# Revit family: KingswayGroup_Shlvs_Anti-LigatureWashroomShelfRecessed
name_source: partatom
category: Specialty Equipment
units: mm (PartAtom-declared; Revit-internal decimal feet)

## family parameters
Always vertical = Yes
Cut with Voids When Loaded = No
Part Type = Normal
Room Calculation Point = No
Round Connector Dimension = Use Diameter
Shared = No
Work Plane-Based = No

## types (1)
- KingswayGroup_Shlvs_Anti-LigatureWashroomShelfRecessed
    AssetType = Fixed
    BIMObjectName = KingswayGroup_Shelves_Anti-LigatureWashroomShelfRecessed
    Category = Pr_40_30_78_78:Shelves
    Color = For full range of available finishes and colours, contact Kingsway Group
    Default Elevation = 0 mm  [stored 0 ft]
    Description = Recessed Washroom Shelf
    DurationUnit = year
    Features = A recessed Anti-Ligature Shelf designed for safe use in patient washrooms, manufactured from 316 grade stainless steel. With elegant and modern aesthetics, the KG12 Anti-Ligature Shelf features a self-draining base making it suitable for holding items such as soap in wet environments.
    Finish = For full range of available finishes and colours, contact Kingsway Group
    Grade = 316
    IfcExportAs = IfcFurnitureType
    IfcExportType = SHELF
    Manufacturer = Kingsway Group
    ManufacturerName = Kingsway Group
    ManufacturerURL = https://kingswaygroupglobal.com
    Material = Stainless Steel
    Model = KG12
    ModelNumber = KG12
    ModelReference = Anti-Ligature Washroom Shelf
    Name = Shelves_Anti-LigatureWashroomShelf_KG12_KingswayGroup
    NominalHeight = 305 mm
    NominalLength = 254 mm
    NominalWidth = 90 mm  [stored 0.295276 ft]
    ProductInformation = https://kingswaygroupglobal.com
    ShelfMaterial = NBS_Concept
    Size = 254 x 304.8 x 90 mm
    URL = https://kingswaygroupglobal.com
    Uniclass2015Code = Pr_40_30_78_78
    Uniclass2015Title = Shelves
    Uniclass2015Version = Products v1.36
    Version = 1
    WarrantyDescription = 5-Year Guarantee *For faulty manufacture and not for damage
    WarrantyDurationParts = 5
    WarrantyDurationUnit = year

note: [stored X ft] marks values corroborated as IEEE doubles in the binary element streams (Revit-internal decimal feet)

## geometry (parser evidence)
native form markers: Sweep x2
no freeform markers — native parametric forms only
